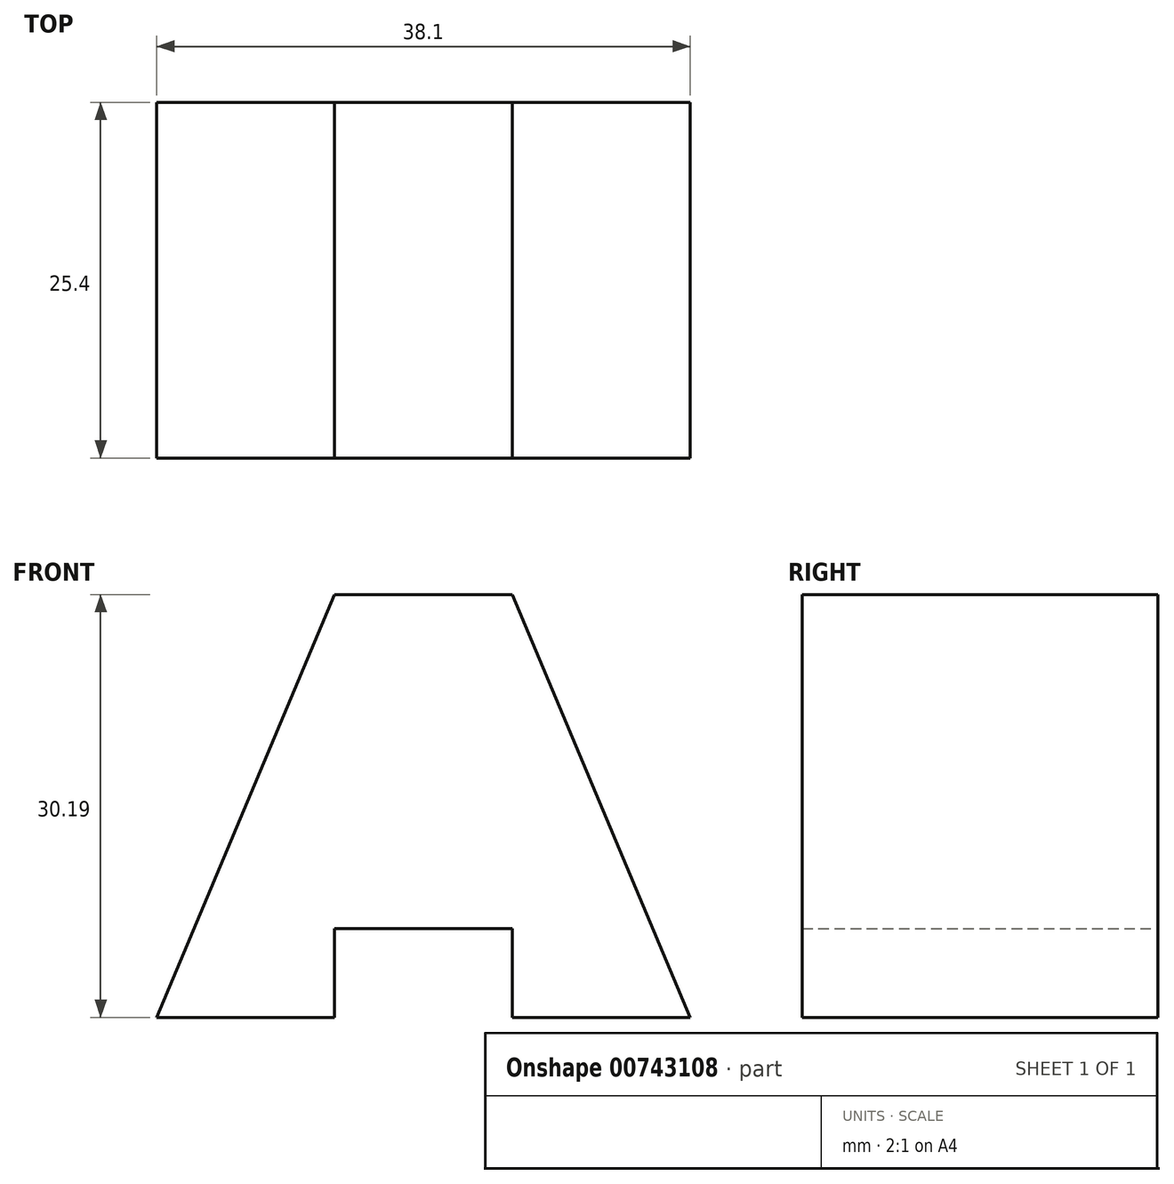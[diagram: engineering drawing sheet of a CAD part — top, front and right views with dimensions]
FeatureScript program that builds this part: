
annotation { "Feature Type Name" : "Feature", "Feature Type Description" : "" }
export const myFeature = defineFeature(function(context is Context, id is Id, definition is map)
    precondition{}
    {
        {
            var Q0;
            Q0=qCreatedBy(makeId("Front.planeOp"),FACE);
            var sketch = newSketch(context, id + "F0", { "sketchPlane" : qUnion([Q0])});
            skLineSegment(sketch, "E0", {"start": v(0, 0) * mm, "end": v(12.7, 0) * mm});
            skLineSegment(sketch, "E1", {"start": v(12.7, 0) * mm, "end": v(12.7, 6.35) * mm});
            skLineSegment(sketch, "E2", {"start": v(12.7, 6.35) * mm, "end": v(25.4, 6.35) * mm});
            skLineSegment(sketch, "E3", {"start": v(25.4, 6.35) * mm, "end": v(25.4, 0) * mm});
            skLineSegment(sketch, "E4", {"start": v(25.4, 0) * mm, "end": v(38.1, 0) * mm});
            skLineSegment(sketch, "E5", {"start": v(38.1, 0) * mm, "end": v(25.4, 30.2) * mm});
            skLineSegment(sketch, "E6", {"start": v(25.4, 30.2) * mm, "end": v(12.7, 30.2) * mm});
            skLineSegment(sketch, "E7", {"start": v(12.7, 30.2) * mm, "end": v(0, 0) * mm});
            skSolve(sketch);
        }
        {
            var Q0;
            Q0=makeQuery(id+"F0.imprint","IMPRINT",FACE,{"disambiguationData":[TD([[makeQuery(id+"F0.imprint","IMPRINT",EDGE,{"derivedFrom":sQuery(id+"F0.wireOp",EDGE,"E0")}),1.0]])]});
            extrude(context, id + "F1", {"entities" : qUnion([Q0]), "depth" : 25.4 * mm, "offsetDistance" : 25.4 * mm});
        }
    });
